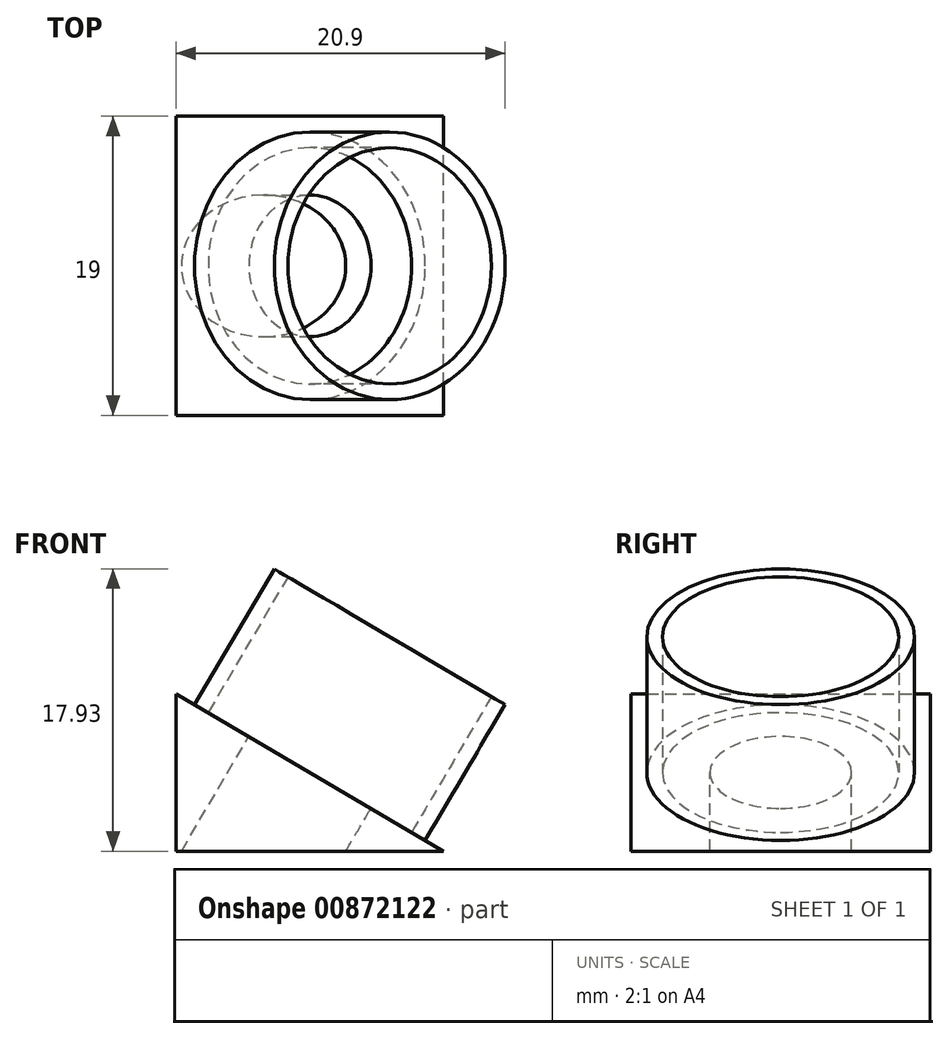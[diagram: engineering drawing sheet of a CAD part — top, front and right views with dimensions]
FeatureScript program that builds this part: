
annotation { "Feature Type Name" : "Feature", "Feature Type Description" : "" }
export const myFeature = defineFeature(function(context is Context, id is Id, definition is map)
    precondition{}
    {
        {
            var Q0;
            Q0=qCreatedBy(makeId("Front.planeOp"),FACE);
            var sketch = newSketch(context, id + "F0", { "sketchPlane" : qUnion([Q0])});
            skLineSegment(sketch, "E0", {"start": v(0, 0) * mm, "end": v(17, 0) * mm});
            skLineSegment(sketch, "E1", {"start": v(0, 0) * mm, "end": v(0, 10) * mm});
            skLineSegment(sketch, "E2", {"start": v(0, 10) * mm, "end": v(17, 0) * mm});
            skSolve(sketch);
        }
        {
            var Q0;
            Q0 = qSketchRegion(id + "F0", true);
            extrude(context, id + "F1", {"entities" : qUnion([Q0]), "depth" : 19 * mm, "offsetDistance" : 25 * mm});
        }
        {
            var Q0;
            Q0=makeQuery(id+"F1.opExtrude","SWEPT_FACE",FACE,{"disambiguationData":[OSD([sQuery(id+"F0.wireOp",EDGE,"E2")])]});
            var sketch = newSketch(context, id + "F2", { "sketchPlane" : qUnion([Q0])});
            skLineSegment(sketch, "E3", {"start": v(4.8, 0) * mm, "end": v(4.8, -19) * mm, "construction": true});
            skPoint(sketch, "E4", {"position": v(4.8, -9.5) * mm});
            skCircle(sketch, "E5", {"center": v(4.8, -9.5) * mm, "radius": 8.5 * mm});
            skCircle(sketch, "E6", {"center": v(4.8, -9.5) * mm, "radius": 7.5 * mm});
            skSolve(sketch);
        }
        {
            var Q0;
            Q0=sQuery(id+"F2.wireOp",VERTEX,"E4");
            var Q1;
            Q1=makeQuery(id+"F1.opExtrude","SWEPT_BODY",BODY,{"disambiguationData":[OSD([sQuery(id+"F0.wireOp",EDGE,"E0"),sQuery(id+"F0.wireOp",EDGE,"E1"),sQuery(id+"F0.wireOp",EDGE,"E2")])]});
            hole(context, id + "F3", {"style" : HoleStyle.SIMPLE, "endStyle" : HoleEndStyle.BLIND, "holeDiameter" : 9 * mm, "majorDiameter" : 5 * mm, "holeDepth" : 30 * mm, "isTappedThrough" : true, "tappedDepth" : 12 * mm, "tapClearance" : 3, "locations" : qUnion([Q0]), "scope" : qUnion([Q1])});
        }
        {
            var Q0;
            Q0=makeQuery(id+"F2.imprint","IMPRINT",FACE,{"disambiguationData":[TD([[makeQuery(id+"F2.imprint","IMPRINT",EDGE,{"derivedFrom":sQuery(id+"F2.wireOp",EDGE,"E5")}),1.0]])]});
            extrude(context, id + "F4", {"entities" : qUnion([Q0]), "operationType" : NewBodyOperationType.ADD, "depth" : 10 * mm, "offsetDistance" : 25 * mm});
        }
    });
